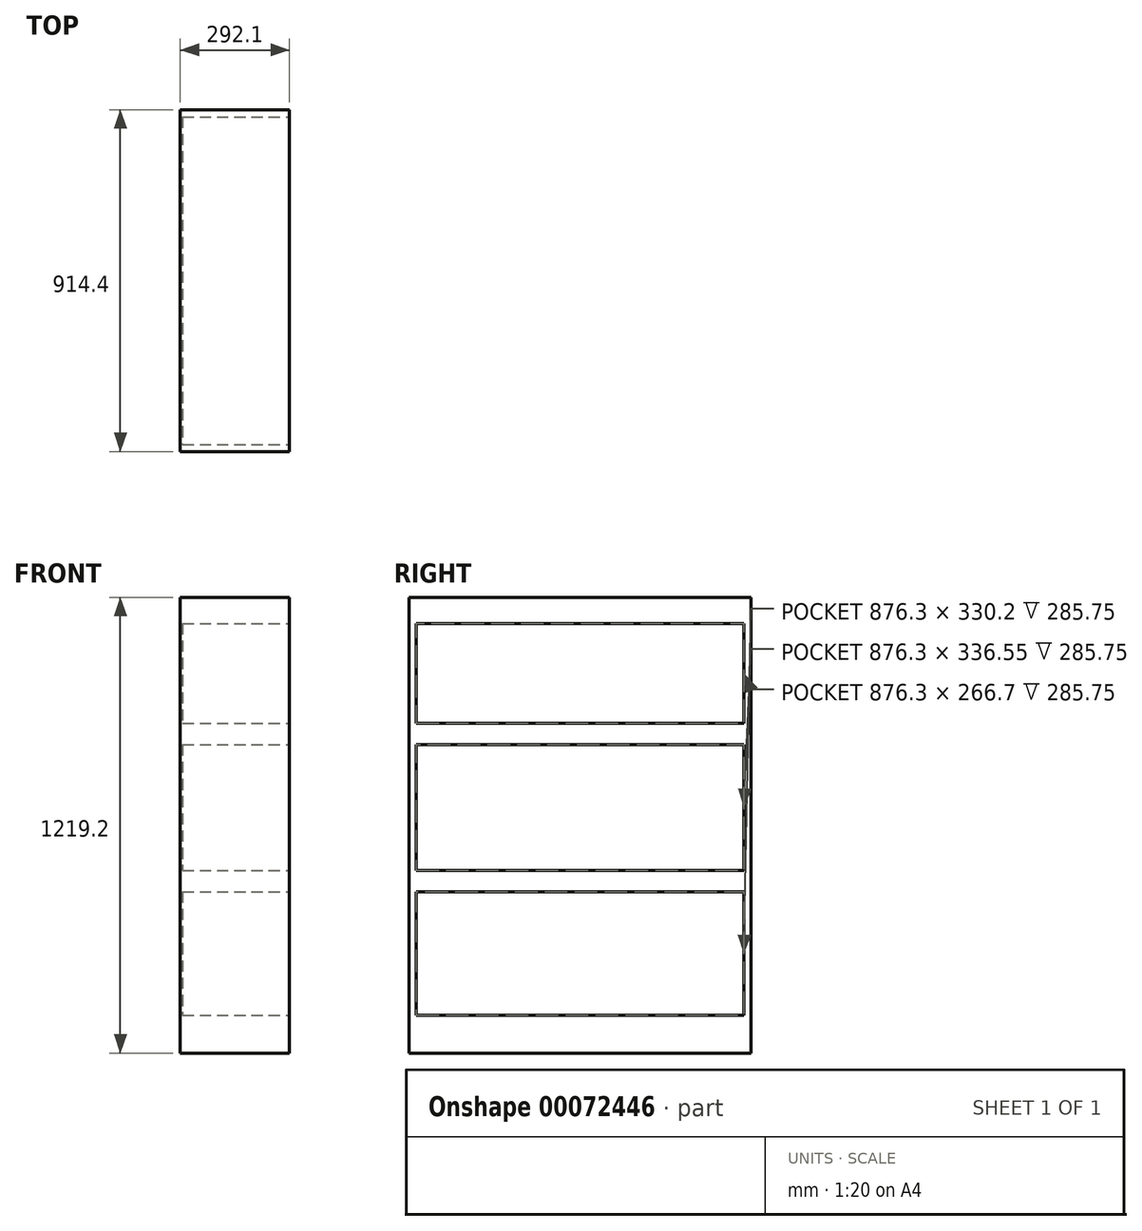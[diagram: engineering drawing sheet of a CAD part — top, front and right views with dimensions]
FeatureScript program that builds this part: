
annotation { "Feature Type Name" : "Feature", "Feature Type Description" : "" }
export const myFeature = defineFeature(function(context is Context, id is Id, definition is map)
    precondition{}
    {
        {
            var Q0;
            Q0=qCreatedBy(makeId("Top.planeOp"),FACE);
            var sketch = newSketch(context, id + "F0", { "sketchPlane" : qUnion([Q0])});
            skLineSegment(sketch, "E0.bottom", {"start": v(0, 457.2) * mm, "end": v(292.1, 457.2) * mm});
            skLineSegment(sketch, "E0.top", {"start": v(0, -457.2) * mm, "end": v(292.1, -457.2) * mm});
            skLineSegment(sketch, "E0.left", {"start": v(0, 457.2) * mm, "end": v(0, -457.2) * mm});
            skLineSegment(sketch, "E0.right", {"start": v(292.1, 457.2) * mm, "end": v(292.1, -457.2) * mm});
            skSolve(sketch);
        }
        {
            var Q0;
            Q0 = qSketchRegion(id + "F0", true);
            extrude(context, id + "F1", {"entities" : qUnion([Q0]), "depth" : 1219.2 * mm});
        }
        {
            var Q0;
            Q0=makeQuery(id+"F1.opExtrude","SWEPT_FACE",FACE,{"disambiguationData":[OSD([sQuery(id+"F0.wireOp",EDGE,"E0.right")])]});
            var sketch = newSketch(context, id + "F2", { "sketchPlane" : qUnion([Q0])});
            skLineSegment(sketch, "E1.rect.bottom", {"start": v(438.15, 1149.35) * mm, "end": v(-438.15, 1149.35) * mm});
            skLineSegment(sketch, "E1.rect.top", {"start": v(438.15, 882.65) * mm, "end": v(-438.15, 882.65) * mm});
            skLineSegment(sketch, "E1.rect.left", {"start": v(438.15, 1149.35) * mm, "end": v(438.15, 882.65) * mm});
            skLineSegment(sketch, "E1.rect.right", {"start": v(-438.15, 1149.35) * mm, "end": v(-438.15, 882.65) * mm});
            skPoint(sketch, "E1.rect.middle", {"position": v(0, 1016) * mm});
            skLineSegment(sketch, "E2.rect.bottom", {"start": v(438.15, 825.5) * mm, "end": v(-438.15, 825.5) * mm});
            skLineSegment(sketch, "E2.rect.top", {"start": v(438.15, 488.95) * mm, "end": v(-438.15, 488.95) * mm});
            skLineSegment(sketch, "E2.rect.left", {"start": v(438.15, 825.5) * mm, "end": v(438.15, 488.95) * mm});
            skLineSegment(sketch, "E2.rect.right", {"start": v(-438.15, 825.5) * mm, "end": v(-438.15, 488.95) * mm});
            skPoint(sketch, "E2.rect.middle", {"position": v(0, 657.23) * mm});
            skLineSegment(sketch, "E3.rect.bottom", {"start": v(438.15, 431.8) * mm, "end": v(-438.15, 431.8) * mm});
            skLineSegment(sketch, "E3.rect.top", {"start": v(438.15, 101.6) * mm, "end": v(-438.15, 101.6) * mm});
            skLineSegment(sketch, "E3.rect.left", {"start": v(438.15, 431.8) * mm, "end": v(438.15, 101.6) * mm});
            skLineSegment(sketch, "E3.rect.right", {"start": v(-438.15, 431.8) * mm, "end": v(-438.15, 101.6) * mm});
            skPoint(sketch, "E3.rect.middle", {"position": v(0, 266.7) * mm});
            skLineSegment(sketch, "E4", {"start": v(-438.15, 882.65) * mm, "end": v(-438.15, 825.5) * mm, "construction": true});
            skLineSegment(sketch, "E5", {"start": v(-438.15, 488.95) * mm, "end": v(-438.15, 431.8) * mm, "construction": true});
            skSolve(sketch);
        }
        {
            var Q0;
            Q0 = qSketchRegion(id + "F2", true);
            extrude(context, id + "F3", {"entities" : qUnion([Q0]), "operationType" : NewBodyOperationType.REMOVE, "oppositeDirection" : true, "depth" : 285.75 * mm});
        }
    });
